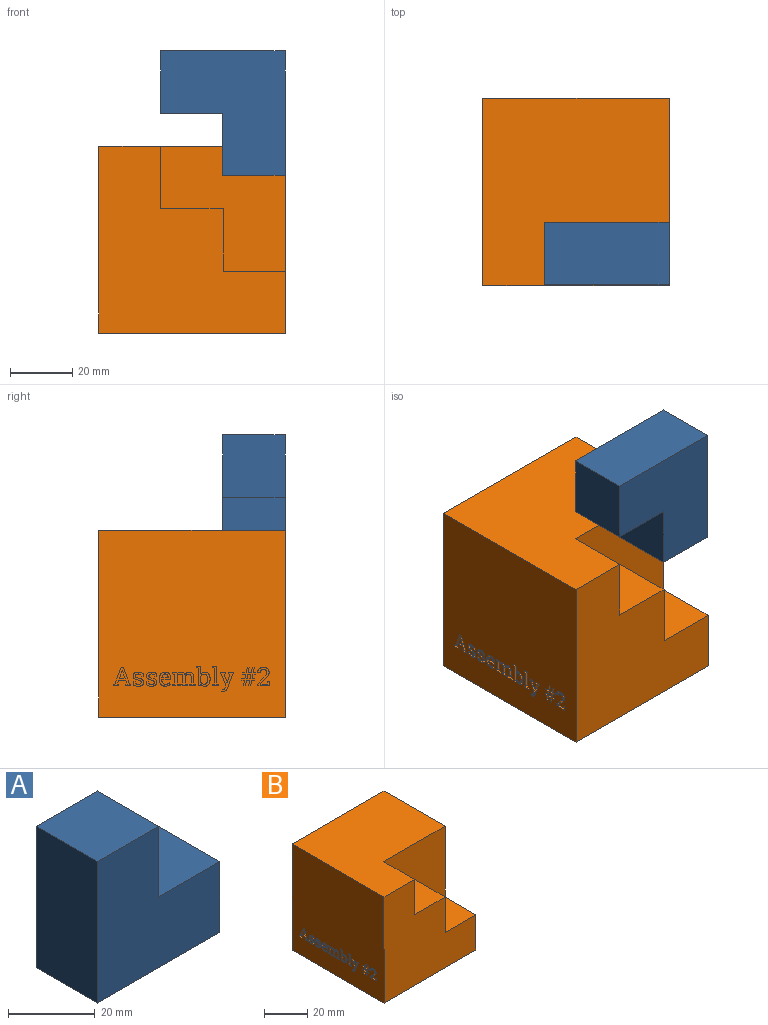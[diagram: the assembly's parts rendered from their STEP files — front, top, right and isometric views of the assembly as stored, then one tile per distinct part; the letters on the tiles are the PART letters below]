
ASSEMBLY  parts=2 mates=2
PART A: 8 faces, bbox 40x20x40 mm
  f0: plane 40x20mm, normal (0,0,-1), area 800mm2, adj f1,f5,f6,f7
  f1: plane 20x20mm, normal (1,0,0), area 400mm2, adj f0,f2,f6,f7
  f2: plane 20x20mm, normal (0,0,1), area 400mm2, adj f1,f3,f6,f7
  f3: plane 20x20mm, normal (1,0,0), area 400mm2, adj f2,f4,f6,f7
  f4: plane 20x20mm, normal (0,0,1), area 400mm2, adj f3,f5,f6,f7
  f5: plane 40x20mm, normal (-1,0,0), area 800mm2, adj f0,f4,f6,f7
  f6: plane 40x40mm, normal (0,-1,0), area 1200mm2, adj f0,f1,f2,f3,f4,f5
  f7: plane 40x40mm, normal (0,1,0), area 1200mm2, adj f0,f1,f2,f3,f4,f5
PART B: 287 faces, bbox 60x60x60 mm
  f0: plane 60x60mm, normal (-1,0,0), area 3490.7mm2, adj f1,f2,f4,f5,f11,f12,f13,f14
  f1: plane 60x60mm, normal (0,0,1), area 2794mm2, adj f0,f3,f4,f5,f6,f10
  f2: plane 60x60mm, normal (0,0,-1), area 3600mm2, adj f0,f3,f4,f5
  f3: plane 60x60mm, normal (1,0,0), area 2794mm2, adj f1,f2,f4,f5,f9,f10
  f4: plane 60x60mm, normal (0,-1,0), area 2396mm2, adj f0,f1,f2,f3,f6,f7,f8,f9
  f5: plane 60x60mm, normal (0,1,0), area 3600mm2, adj f0,f1,f2,f3
  f6: plane 20.1x20mm, normal (1,0,0), area 402mm2, adj f1,f4,f7,f10
  f7: plane 20.1x20.1mm, normal (0,0,1), area 404mm2, adj f4,f6,f8,f10
  f8: plane 20.1x20.1mm, normal (1,0,0), area 404mm2, adj f4,f7,f9,f10
  f9: plane 20.1x20mm, normal (0,0,1), area 402mm2, adj f3,f4,f8,f10
  f10: plane 40.1x40.1mm, normal (0,-1,0), area 1204mm2, adj f1,f3,f6,f7,f8,f9
  f11: plane 3x0.6mm, normal (0,0,1), area 1.8mm2, adj f0,f12,f40,f41
  f12: plane 3x0.97mm, normal (0,1,-0.04), area 2.9mm2, adj f0,f11,f13,f41
  f13: extruded ~3x0.66mm, area 2.3mm2, adj f0,f12,f14,f41
  f14: extruded ~3x0.9mm, area 2.7mm2, adj f0,f13,f15,f41
  f15: extruded ~3x1.19mm, area 3.8mm2, adj f0,f14,f16,f41
  f16: extruded ~3x0.92mm, area 3.2mm2, adj f0,f15,f17,f41
  f17: extruded ~3x0.81mm, area 2.8mm2, adj f0,f16,f18,f41
  f18: extruded ~3x1.21mm, area 3.9mm2, adj f0,f17,f19,f41
  f19: extruded ~3x0.76mm, area 2.5mm2, adj f0,f18,f20,f41
  f20: extruded ~3x0.44mm, area 1.5mm2, adj f0,f19,f21,f41
  f21: extruded ~3x0.45mm, area 1.6mm2, adj f0,f20,f22,f41
  f22: extruded ~3x0.67mm, area 2.1mm2, adj f0,f21,f23,f41
  f23: extruded ~3x0.49mm, area 1.5mm2, adj f0,f22,f24,f41
  f24: extruded ~3x0.38mm, area 1.3mm2, adj f0,f23,f25,f41
  f25: plane 3x0.59mm, normal (0,0.97,-0.25), area 1.8mm2, adj f0,f24,f26,f41
  f26: plane 3x0.6mm, normal (0,0,-1), area 1.8mm2, adj f0,f25,f27,f41
  f27: plane 3x1.01mm, normal (0,-1,0.01), area 3mm2, adj f0,f26,f28,f41
  f28: extruded ~3x0.71mm, area 2.4mm2, adj f0,f27,f29,f41
  f29: extruded ~3x0.9mm, area 2.7mm2, adj f0,f28,f30,f41
  f30: extruded ~3x1.24mm, area 3.9mm2, adj f0,f29,f31,f41
  f31: extruded ~3x0.95mm, area 3.3mm2, adj f0,f30,f32,f41
  f32: extruded ~3x0.82mm, area 2.9mm2, adj f0,f31,f33,f41
  f33: extruded ~3x1.24mm, area 4mm2, adj f0,f32,f34,f41
  f34: extruded ~3x0.74mm, area 2.4mm2, adj f0,f33,f35,f41
  f35: extruded ~3x0.41mm, area 1.4mm2, adj f0,f34,f36,f41
  f36: extruded ~3x0.45mm, area 1.5mm2, adj f0,f35,f37,f41
  f37: extruded ~3x0.63mm, area 2mm2, adj f0,f36,f38,f41
  f38: extruded ~3x0.5mm, area 1.5mm2, adj f0,f37,f39,f41
  f39: extruded ~3x0.37mm, area 1.3mm2, adj f0,f38,f40,f41
  f40: plane 3x0.53mm, normal (0,-0.97,0.24), area 1.6mm2, adj f0,f11,f39,f41
  f41: plane 4.57x3.38mm, normal (-1,0,0), area 7.9mm2, adj f11,f12,f13,f14,f15,f16,f17,f18
  f42: plane 3x1.04mm, normal (0,0,-1), area 3.1mm2, adj f43,f73,f74,f283
  f43: plane 3x1.42mm, normal (0,0.98,0.19), area 4.3mm2, adj f42,f44,f74,f283
  f44: plane 3x1.04mm, normal (0,0,1), area 3.1mm2, adj f43,f73,f74,f283
  f45: plane 3x1.04mm, normal (0,0,1), area 3.1mm2, adj f0,f46,f72,f74
  f46: plane 3x1.67mm, normal (0,-0.98,-0.19), area 5.1mm2, adj f0,f45,f47,f74
  f47: plane 3x0.61mm, normal (0,0,1), area 1.8mm2, adj f0,f46,f48,f74
  f48: plane 3x1.67mm, normal (0,0.98,0.19), area 5.1mm2, adj f0,f47,f49,f74
  f49: plane 3x1.01mm, normal (0,0,1), area 3mm2, adj f0,f48,f50,f74
  f50: plane 3x0.57mm, normal (0,1,0), area 1.7mm2, adj f0,f49,f51,f74
  f51: plane 3x0.89mm, normal (0,0,-1), area 2.7mm2, adj f0,f50,f52,f74
  f52: plane 3x1.42mm, normal (0,0.98,0.19), area 4.3mm2, adj f0,f51,f53,f74
  f53: plane 3x0.92mm, normal (0,0,1), area 2.8mm2, adj f0,f52,f54,f74
  f54: plane 3x0.58mm, normal (0,1,0), area 1.7mm2, adj f0,f53,f55,f74
  f55: plane 3x0.81mm, normal (0,0,-1), area 2.4mm2, adj f0,f54,f56,f74
  f56: plane 3x1.69mm, normal (0,0.98,0.19), area 5.2mm2, adj f0,f55,f57,f74
  f57: plane 3x0.61mm, normal (0,0,-1), area 1.8mm2, adj f0,f56,f58,f74
  f58: plane 3x1.69mm, normal (0,-0.98,-0.19), area 5.2mm2, adj f0,f57,f59,f74
  f59: plane 3x1.04mm, normal (0,0,-1), area 3.1mm2, adj f0,f58,f60,f74
  f60: plane 3x1.69mm, normal (0,0.98,0.19), area 5.2mm2, adj f0,f59,f61,f74
  f61: plane 3x0.61mm, normal (0,0,-1), area 1.8mm2, adj f0,f60,f62,f74
  f62: plane 3x1.69mm, normal (0,-0.98,-0.19), area 5.2mm2, adj f0,f61,f63,f74
  f63: plane 3x1.15mm, normal (0,0,-1), area 3.5mm2, adj f0,f62,f64,f74
  f64: plane 3x0.58mm, normal (0,-1,0), area 1.7mm2, adj f0,f63,f65,f74
  f65: plane 3x1.04mm, normal (0,0,1), area 3.1mm2, adj f0,f64,f66,f74
  f66: plane 3x1.42mm, normal (0,-0.98,-0.19), area 4.3mm2, adj f0,f65,f67,f74
  f67: plane 3x1.07mm, normal (0,0,-1), area 3.2mm2, adj f0,f66,f68,f74
  f68: plane 3x0.57mm, normal (0,-1,0), area 1.7mm2, adj f0,f67,f69,f74
  f69: plane 3x0.96mm, normal (0,0,1), area 2.9mm2, adj f0,f68,f70,f74
  f70: plane 3x1.67mm, normal (0,-0.98,-0.19), area 5.1mm2, adj f0,f69,f71,f74
  f71: plane 3x0.61mm, normal (0,0,1), area 1.8mm2, adj f0,f70,f72,f74
  f72: plane 3x1.67mm, normal (0,0.98,0.19), area 5.1mm2, adj f0,f45,f71,f74
  f73: plane 3x1.42mm, normal (0,-0.98,-0.19), area 4.3mm2, adj f42,f44,f74,f283
  f74: plane 5.92x4.54mm, normal (-1,0,0), area 10.7mm2, adj f42,f43,f44,f45,f46,f47,f48,f49
  f75: plane 3x0.6mm, normal (0,0,1), area 1.8mm2, adj f0,f76,f104,f105
  f76: plane 3x0.97mm, normal (0,1,-0.04), area 2.9mm2, adj f0,f75,f77,f105
  f77: extruded ~3x0.66mm, area 2.3mm2, adj f0,f76,f78,f105
  f78: extruded ~3x0.9mm, area 2.7mm2, adj f0,f77,f79,f105
  f79: extruded ~3x1.19mm, area 3.8mm2, adj f0,f78,f80,f105
  f80: extruded ~3x0.92mm, area 3.2mm2, adj f0,f79,f81,f105
  f81: extruded ~3x0.81mm, area 2.8mm2, adj f0,f80,f82,f105
  f82: extruded ~3x1.21mm, area 3.9mm2, adj f0,f81,f83,f105
  f83: extruded ~3x0.76mm, area 2.5mm2, adj f0,f82,f84,f105
  f84: extruded ~3x0.44mm, area 1.5mm2, adj f0,f83,f85,f105
  f85: extruded ~3x0.45mm, area 1.6mm2, adj f0,f84,f86,f105
  f86: extruded ~3x0.67mm, area 2.1mm2, adj f0,f85,f87,f105
  f87: extruded ~3x0.49mm, area 1.5mm2, adj f0,f86,f88,f105
  f88: extruded ~3x0.38mm, area 1.3mm2, adj f0,f87,f89,f105
  f89: plane 3x0.59mm, normal (0,0.97,-0.25), area 1.8mm2, adj f0,f88,f90,f105
  f90: plane 3x0.6mm, normal (0,0,-1), area 1.8mm2, adj f0,f89,f91,f105
  f91: plane 3x1.01mm, normal (0,-1,0.01), area 3mm2, adj f0,f90,f92,f105
  f92: extruded ~3x0.71mm, area 2.4mm2, adj f0,f91,f93,f105
  f93: extruded ~3x0.9mm, area 2.7mm2, adj f0,f92,f94,f105
  f94: extruded ~3x1.24mm, area 3.9mm2, adj f0,f93,f95,f105
  f95: extruded ~3x0.95mm, area 3.3mm2, adj f0,f94,f96,f105
  f96: extruded ~3x0.82mm, area 2.9mm2, adj f0,f95,f97,f105
  f97: extruded ~3x1.24mm, area 4mm2, adj f0,f96,f98,f105
  f98: extruded ~3x0.74mm, area 2.4mm2, adj f0,f97,f99,f105
  f99: extruded ~3x0.41mm, area 1.4mm2, adj f0,f98,f100,f105
  f100: extruded ~3x0.45mm, area 1.5mm2, adj f0,f99,f101,f105
  f101: extruded ~3x0.63mm, area 2mm2, adj f0,f100,f102,f105
  f102: extruded ~3x0.5mm, area 1.5mm2, adj f0,f101,f103,f105
  f103: extruded ~3x0.37mm, area 1.3mm2, adj f0,f102,f104,f105
  f104: plane 3x0.53mm, normal (0,-0.97,0.24), area 1.6mm2, adj f0,f75,f103,f105
  f105: plane 4.57x3.38mm, normal (-1,0,0), area 7.9mm2, adj f75,f76,f77,f78,f79,f80,f81,f82
  f106: plane 3x0.66mm, normal (0,-0.17,-0.99), area 2mm2, adj f0,f107,f146,f147
  f107: plane 3x0.51mm, normal (0,-1,0), area 1.5mm2, adj f0,f106,f108,f147
  f108: plane 3x2.13mm, normal (0,0,1), area 6.4mm2, adj f0,f107,f109,f147
  f109: plane 3x0.51mm, normal (0,1,0), area 1.5mm2, adj f0,f108,f110,f147
  f110: plane 3x0.66mm, normal (0,0.17,-0.99), area 2mm2, adj f0,f109,f111,f147
  f111: plane 3x2.63mm, normal (0,1,0), area 7.9mm2, adj f0,f110,f112,f147
  f112: extruded ~3x0.42mm, area 1.7mm2, adj f0,f111,f113,f147
  f113: extruded ~3x0.6mm, area 1.9mm2, adj f0,f112,f114,f147
  f114: extruded ~3x0.66mm, area 2.3mm2, adj f0,f113,f115,f147
  f115: extruded ~3x0.91mm, area 2.9mm2, adj f0,f114,f116,f147
  f116: plane 3x2.01mm, normal (0,-1,0), area 6mm2, adj f0,f115,f117,f147
  f117: plane 3x0.66mm, normal (0,-0.17,-0.99), area 2mm2, adj f0,f116,f118,f147
  f118: plane 3x0.51mm, normal (0,-1,0), area 1.5mm2, adj f0,f117,f119,f147
  f119: plane 3x2.13mm, normal (0,0,1), area 6.4mm2, adj f0,f118,f120,f147
  f120: plane 3x0.51mm, normal (0,1,0), area 1.5mm2, adj f0,f119,f121,f147
  f121: plane 3x0.66mm, normal (0,0.17,-0.99), area 2mm2, adj f0,f120,f122,f147
  f122: plane 3x2.17mm, normal (0,1,0), area 6.5mm2, adj f0,f121,f123,f147
  f123: extruded ~3x0.74mm, area 2.4mm2, adj f0,f122,f124,f147
  f124: extruded ~3x0.67mm, area 2.3mm2, adj f0,f123,f125,f147
  f125: extruded ~3x0.66mm, area 2.2mm2, adj f0,f124,f126,f147
  f126: extruded ~3x0.92mm, area 2.9mm2, adj f0,f125,f127,f147
  f127: plane 3x2.01mm, normal (0,-1,0), area 6mm2, adj f0,f126,f128,f147
  f128: plane 3x0.66mm, normal (0,-0.17,-0.99), area 2mm2, adj f0,f127,f129,f147
  f129: plane 3x0.51mm, normal (0,-1,0), area 1.5mm2, adj f0,f128,f130,f147
  f130: plane 3x2.13mm, normal (0,0,1), area 6.4mm2, adj f0,f129,f131,f147
  f131: plane 3x0.51mm, normal (0,1,0), area 1.5mm2, adj f0,f130,f132,f147
  f132: plane 3x0.66mm, normal (0,0.17,-0.99), area 2mm2, adj f0,f131,f133,f147
  f133: plane 3x2.01mm, normal (0,1,0), area 6mm2, adj f0,f132,f134,f147
  f134: extruded ~3x1.39mm, area 4.4mm2, adj f0,f133,f135,f147
  f135: extruded ~3x1.07mm, area 3.6mm2, adj f0,f134,f136,f147
  f136: extruded ~3x0.8mm, area 2.5mm2, adj f0,f135,f137,f147
  f137: extruded ~3x0.59mm, area 2.5mm2, adj f0,f136,f138,f147
  f138: extruded ~3x0.61mm, area 2.4mm2, adj f0,f137,f139,f147
  f139: extruded ~3x0.75mm, area 2.4mm2, adj f0,f138,f140,f147
  f140: extruded ~3x0.77mm, area 2.4mm2, adj f0,f139,f141,f147
  f141: extruded ~3x0.55mm, area 2.2mm2, adj f0,f140,f142,f147
  f142: plane 3x0.57mm, normal (0,1,-0.09), area 1.7mm2, adj f0,f141,f143,f147
  f143: plane 3x1.38mm, normal (0,0,-1), area 4.2mm2, adj f0,f142,f144,f147
  f144: plane 3x0.52mm, normal (0,-1,0), area 1.6mm2, adj f0,f143,f145,f147
  f145: plane 3x0.66mm, normal (0,-0.17,0.99), area 2mm2, adj f0,f144,f146,f147
  f146: plane 3.15x3mm, normal (0,-1,0), area 9.4mm2, adj f0,f106,f145,f147
  f147: plane 7.45x4.48mm, normal (-1,0,0), area 15.2mm2, adj f106,f107,f108,f109,f110,f111,f112,f113
  f148: plane 3x0.52mm, normal (0,-1,0), area 1.6mm2, adj f0,f149,f157,f158
  f149: plane 3x0.66mm, normal (0,-0.17,0.99), area 2mm2, adj f0,f148,f150,f158
  f150: plane 5.09x3mm, normal (0,-1,0), area 15.3mm2, adj f0,f149,f151,f158
  f151: plane 3x0.66mm, normal (0,-0.17,-0.99), area 2mm2, adj f0,f150,f152,f158
  f152: plane 3x0.51mm, normal (0,-1,0), area 1.5mm2, adj f0,f151,f153,f158
  f153: plane 3x2.13mm, normal (0,0,1), area 6.4mm2, adj f0,f152,f154,f158
  f154: plane 3x0.51mm, normal (0,1,0), area 1.5mm2, adj f0,f153,f155,f158
  f155: plane 3x0.66mm, normal (0,0.17,-0.99), area 2mm2, adj f0,f154,f156,f158
  f156: plane 5.72x3mm, normal (0,1,0), area 17.2mm2, adj f0,f155,f157,f158
  f157: plane 3x1.47mm, normal (0,0,-1), area 4.4mm2, adj f0,f148,f156,f158
  f158: plane 6.35x2.13mm, normal (-1,0,0), area 6.2mm2, adj f148,f149,f150,f151,f152,f153,f154,f155
  f159: plane 3x0.39mm, normal (0,0.15,0.99), area 1.2mm2, adj f0,f160,f184,f185
  f160: plane 3x0.52mm, normal (0,1,0), area 1.6mm2, adj f0,f159,f161,f185
  f161: plane 3x1.77mm, normal (0,0,-1), area 5.3mm2, adj f0,f160,f162,f185
  f162: plane 3x0.52mm, normal (0,-1,0), area 1.6mm2, adj f0,f161,f163,f185
  f163: plane 3x0.5mm, normal (0,-0.16,0.99), area 1.5mm2, adj f0,f162,f164,f185
  f164: plane 3x2.73mm, normal (0,-0.95,-0.32), area 8.7mm2, adj f0,f163,f165,f185
  f165: plane 3x0.02mm, normal (0,0,-1), area 0.1mm2, adj f0,f164,f166,f185
  f166: plane 3x0.56mm, normal (0,0.97,-0.25), area 1.7mm2, adj f0,f165,f167,f185
  f167: plane 3x2.17mm, normal (0,0.94,-0.33), area 6.9mm2, adj f0,f166,f168,f185
  f168: plane 3x0.5mm, normal (0,0.16,0.99), area 1.5mm2, adj f0,f167,f169,f185
  f169: plane 3x0.52mm, normal (0,1,0), area 1.6mm2, adj f0,f168,f170,f185
  f170: plane 3x1.78mm, normal (0,0,-1), area 5.3mm2, adj f0,f169,f171,f185
  f171: plane 3x0.52mm, normal (0,-1,0), area 1.6mm2, adj f0,f170,f172,f185
  f172: plane 3x0.4mm, normal (0,-0.16,0.99), area 1.2mm2, adj f0,f171,f173,f185
  f173: plane 3.73x3mm, normal (0,-0.93,0.36), area 12mm2, adj f0,f172,f174,f185
  f174: plane 3x0.46mm, normal (0,-0.92,-0.38), area 1.5mm2, adj f0,f173,f175,f185
  f175: extruded ~3x0.51mm, area 1.7mm2, adj f0,f174,f176,f185
  f176: extruded ~3x0.42mm, area 1.5mm2, adj f0,f175,f177,f185
  f177: extruded ~3x0.21mm, area 0.6mm2, adj f0,f176,f178,f185
  f178: extruded ~3x0.15mm, area 0.5mm2, adj f0,f177,f179,f185
  f179: plane 3x0.63mm, normal (0,-0.99,-0.13), area 1.9mm2, adj f0,f178,f180,f185
  f180: extruded ~3x0.23mm, area 0.7mm2, adj f0,f179,f181,f185
  f181: extruded ~3x0.24mm, area 0.7mm2, adj f0,f180,f182,f185
  f182: extruded ~3x0.84mm, area 2.8mm2, adj f0,f181,f183,f185
  f183: extruded ~3x0.77mm, area 2.7mm2, adj f0,f182,f184,f185
  f184: plane 4.5x3mm, normal (0,0.94,0.35), area 14.4mm2, adj f0,f159,f183,f185
  f185: plane 6.18x4.4mm, normal (-1,0,0), area 9.4mm2, adj f159,f160,f161,f162,f163,f164,f165,f166
  f186: extruded ~3x1.24mm, area 3.8mm2, adj f187,f211,f212,f284
  f187: plane 3x0.08mm, normal (0,-1,0), area 0.3mm2, adj f186,f188,f212,f284
  f188: extruded ~3x1.07mm, area 3.4mm2, adj f187,f189,f212,f284
  f189: extruded ~3x0.84mm, area 2.9mm2, adj f188,f190,f212,f284
  f190: extruded ~3x0.63mm, area 2mm2, adj f189,f191,f212,f284
  f191: extruded ~3x0.49mm, area 1.9mm2, adj f190,f192,f212,f284
  f192: plane 3x1.95mm, normal (0,1,0), area 5.8mm2, adj f191,f193,f212,f284
  f193: extruded ~3x0.48mm, area 1.9mm2, adj f192,f194,f212,f284
  f194: extruded ~3x0.63mm, area 2mm2, adj f193,f211,f212,f284
  f195: extruded ~3x1.54mm, area 4.9mm2, adj f0,f196,f210,f212
  f196: plane 3x0.08mm, normal (0,1,0), area 0.3mm2, adj f0,f195,f197,f212
  f197: extruded ~3x1.71mm, area 5.4mm2, adj f0,f196,f198,f212
  f198: extruded ~3x1.27mm, area 4.5mm2, adj f0,f197,f199,f212
  f199: extruded ~3x0.72mm, area 2.2mm2, adj f0,f198,f200,f212
  f200: extruded ~3x0.51mm, area 2.1mm2, adj f0,f199,f201,f212
  f201: plane 3x2.47mm, normal (0,1,0), area 7.4mm2, adj f0,f200,f202,f212
  f202: plane 3x1.47mm, normal (0,0,-1), area 4.4mm2, adj f0,f201,f203,f212
  f203: plane 3x0.52mm, normal (0,-1,0), area 1.6mm2, adj f0,f202,f204,f212
  f204: plane 3x0.66mm, normal (0,-0.17,0.99), area 2mm2, adj f0,f203,f205,f212
  f205: plane 5.72x3mm, normal (0,-1,0), area 17.2mm2, adj f0,f204,f206,f212
  f206: plane 3x0.69mm, normal (0,0,1), area 2.1mm2, adj f0,f205,f207,f212
  f207: plane 3x0.57mm, normal (0,0.99,0.13), area 1.7mm2, adj f0,f206,f208,f212
  f208: extruded ~3x0.53mm, area 2.2mm2, adj f0,f207,f209,f212
  f209: extruded ~3x0.75mm, area 2.3mm2, adj f0,f208,f210,f212
  f210: extruded ~3x1.26mm, area 4.3mm2, adj f0,f195,f209,f212
  f211: extruded ~3x0.85mm, area 3.1mm2, adj f186,f194,f212,f284
  f212: plane 6.43x4.42mm, normal (-1,0,0), area 11.1mm2, adj f186,f187,f188,f189,f190,f191,f192,f193
  f213: extruded ~3x0.69mm, area 2.4mm2, adj f214,f236,f237,f285
  f214: extruded ~3x0.75mm, area 2.5mm2, adj f213,f215,f237,f285
  f215: extruded ~3x0.79mm, area 2.5mm2, adj f214,f216,f237,f285
  f216: plane 3x0.11mm, normal (0,-1,0), area 0.3mm2, adj f215,f217,f237,f285
  f217: plane 3x2.03mm, normal (0,0,-1), area 6.1mm2, adj f216,f218,f237,f285
  f218: plane 3x0.02mm, normal (0,0.92,-0.4), area 0.1mm2, adj f217,f236,f237,f285
  f219: extruded ~3x1.46mm, area 4.9mm2, adj f0,f220,f235,f237
  f220: extruded ~3x0.93mm, area 2.9mm2, adj f0,f219,f221,f237
  f221: extruded ~3x0.62mm, area 2.2mm2, adj f0,f220,f222,f237
  f222: plane 3x0.52mm, normal (0,0.86,-0.52), area 1.8mm2, adj f0,f221,f223,f237
  f223: extruded ~3x0.53mm, area 1.9mm2, adj f0,f222,f224,f237
  f224: extruded ~3x0.71mm, area 2.2mm2, adj f0,f223,f225,f237
  f225: extruded ~3x0.87mm, area 3mm2, adj f0,f224,f226,f237
  f226: extruded ~3x1.04mm, area 3.3mm2, adj f0,f225,f227,f237
  f227: plane 3x0.02mm, normal (0,0.85,0.53), area 0.1mm2, adj f0,f226,f228,f237
  f228: plane 3x2.86mm, normal (0,0,1), area 8.6mm2, adj f0,f227,f229,f237
  f229: plane 3x0.5mm, normal (0,1,0), area 1.5mm2, adj f0,f228,f230,f237
  f230: extruded ~3x1.43mm, area 4.6mm2, adj f0,f229,f231,f237
  f231: extruded ~3x1.35mm, area 4.5mm2, adj f0,f230,f232,f237
  f232: extruded ~3x1.32mm, area 4.5mm2, adj f0,f231,f233,f237
  f233: extruded ~3x1.56mm, area 5.1mm2, adj f0,f232,f234,f237
  f234: plane 3x0.18mm, normal (0,-1,0), area 0.5mm2, adj f0,f233,f235,f237
  f235: extruded ~3x1.59mm, area 5.2mm2, adj f0,f219,f234,f237
  f236: extruded ~3x0.85mm, area 2.8mm2, adj f213,f218,f237,f285
  f237: plane 4.57x3.69mm, normal (-1,0,0), area 8.5mm2, adj f213,f214,f215,f216,f217,f218,f219,f220
  f238: plane 3x1.88mm, normal (0,0,-1), area 5.6mm2, adj f239,f257,f258,f286
  f239: plane 3x2.54mm, normal (0,0.94,0.35), area 8.1mm2, adj f238,f240,f258,f286
  f240: plane 3x0.02mm, normal (0,0,1), area 0.1mm2, adj f239,f257,f258,f286
  f241: plane 3x0.44mm, normal (0,-0.14,-0.99), area 1.3mm2, adj f0,f242,f256,f258
  f242: plane 3x0.51mm, normal (0,-1,0), area 1.5mm2, adj f0,f241,f243,f258
  f243: plane 3x1.7mm, normal (0,0,1), area 5.1mm2, adj f0,f242,f244,f258
  f244: plane 3x0.51mm, normal (0,1,0), area 1.5mm2, adj f0,f243,f245,f258
  f245: plane 3x0.45mm, normal (0,0.17,-0.99), area 1.4mm2, adj f0,f244,f246,f258
  f246: plane 3x1.09mm, normal (0,0.94,0.35), area 3.5mm2, adj f0,f245,f247,f258
  f247: plane 3x2.37mm, normal (0,0,1), area 7.1mm2, adj f0,f246,f248,f258
  f248: plane 3x1.09mm, normal (0,-0.94,0.34), area 3.5mm2, adj f0,f247,f249,f258
  f249: plane 3x0.45mm, normal (0,-0.17,-0.99), area 1.4mm2, adj f0,f248,f250,f258
  f250: plane 3x0.51mm, normal (0,-1,0), area 1.5mm2, adj f0,f249,f251,f258
  f251: plane 3x1.7mm, normal (0,0,1), area 5.1mm2, adj f0,f250,f252,f258
  f252: plane 3x0.51mm, normal (0,1,0), area 1.5mm2, adj f0,f251,f253,f258
  f253: plane 3x0.44mm, normal (0,0.14,-0.99), area 1.3mm2, adj f0,f252,f254,f258
  f254: plane 5.35x3mm, normal (0,0.93,-0.36), area 17.2mm2, adj f0,f253,f255,f258
  f255: plane 3x0.69mm, normal (0,0,-1), area 2.1mm2, adj f0,f254,f256,f258
  f256: plane 5.35x3mm, normal (0,-0.93,-0.36), area 17.2mm2, adj f0,f241,f255,f258
  f257: plane 3x2.54mm, normal (0,-0.94,0.34), area 8.1mm2, adj f238,f240,f258,f286
  f258: plane 5.92x5.67mm, normal (-1,0,0), area 11.1mm2, adj f238,f239,f240,f241,f242,f243,f244,f245
  f259: plane 3x0.55mm, normal (0,-1,0), area 1.6mm2, adj f0,f260,f281,f282
  f260: plane 3.84x3mm, normal (0,0,1), area 11.5mm2, adj f0,f259,f261,f282
  f261: plane 3x1.31mm, normal (0,1,0), area 3.9mm2, adj f0,f260,f262,f282
  f262: plane 3x0.68mm, normal (0,0,-1), area 2mm2, adj f0,f261,f263,f282
  f263: plane 3x0.68mm, normal (0,-1,-0.1), area 2mm2, adj f0,f262,f264,f282
  f264: plane 3x2.1mm, normal (0,0,-1), area 6.3mm2, adj f0,f263,f265,f282
  f265: plane 3x0.02mm, normal (0,0.92,-0.4), area 0.1mm2, adj f0,f264,f266,f282
  f266: plane 3x1.7mm, normal (0,0.74,0.68), area 6.9mm2, adj f0,f265,f267,f282
  f267: extruded ~3x1.05mm, area 4mm2, adj f0,f266,f268,f282
  f268: extruded ~3x0.97mm, area 3.1mm2, adj f0,f267,f269,f282
  f269: extruded ~3x1.19mm, area 3.9mm2, adj f0,f268,f270,f282
  f270: extruded ~3x1.28mm, area 4.2mm2, adj f0,f269,f271,f282
  f271: extruded ~3x1.46mm, area 4.8mm2, adj f0,f270,f272,f282
  f272: extruded ~3x1.29mm, area 4.3mm2, adj f0,f271,f273,f282
  f273: plane 3x0.02mm, normal (0,-0.95,0.3), area 0.1mm2, adj f0,f272,f274,f282
  f274: plane 3x0.77mm, normal (0,0,1), area 2.3mm2, adj f0,f273,f275,f282
  f275: extruded ~3x0.89mm, area 2.9mm2, adj f0,f274,f276,f282
  f276: extruded ~3x0.9mm, area 3mm2, adj f0,f275,f277,f282
  f277: extruded ~3x0.69mm, area 2.3mm2, adj f0,f276,f278,f282
  f278: extruded ~3x0.75mm, area 2.4mm2, adj f0,f277,f279,f282
  f279: extruded ~3x0.7mm, area 2.2mm2, adj f0,f278,f280,f282
  f280: extruded ~3x0.92mm, area 3.5mm2, adj f0,f279,f281,f282
  f281: plane 3x2.16mm, normal (0,-0.74,-0.67), area 8.7mm2, adj f0,f259,f280,f282
  f282: plane 6.01x3.94mm, normal (-1,0,0), area 9.5mm2, adj f259,f260,f261,f262,f263,f264,f265,f266
  f283: plane 1.42x1.32mm, normal (-1,0,0), area 1.5mm2, adj f42,f43,f44,f73
  f284: plane 3.27x2.15mm, normal (-1,0,0), area 6mm2, adj f186,f187,f188,f189,f190,f191,f192,f193
  f285: plane 2.04x1.21mm, normal (-1,0,0), area 2mm2, adj f213,f214,f215,f216,f217,f218,f236
  f286: plane 2.54x1.88mm, normal (-1,0,0), area 2.4mm2, adj f238,f239,f240,f257
PLACE A rot(axis=(0.71,0,-0.71),180deg) t=(172.55,-1.88,74.42)mm
PLACE B rot(axis=(0.16,-0.69,0.7),0deg) t=(112.65,58.02,-37.15)mm fixed
MATE planar B.f6 <-> A.f4  axis (1,0,0) through (132.55,8.07,12.85)mm
MATE planar B.f10 <-> A.f6  axis (0,-1,0) through (155.96,18.12,6.16)mm
